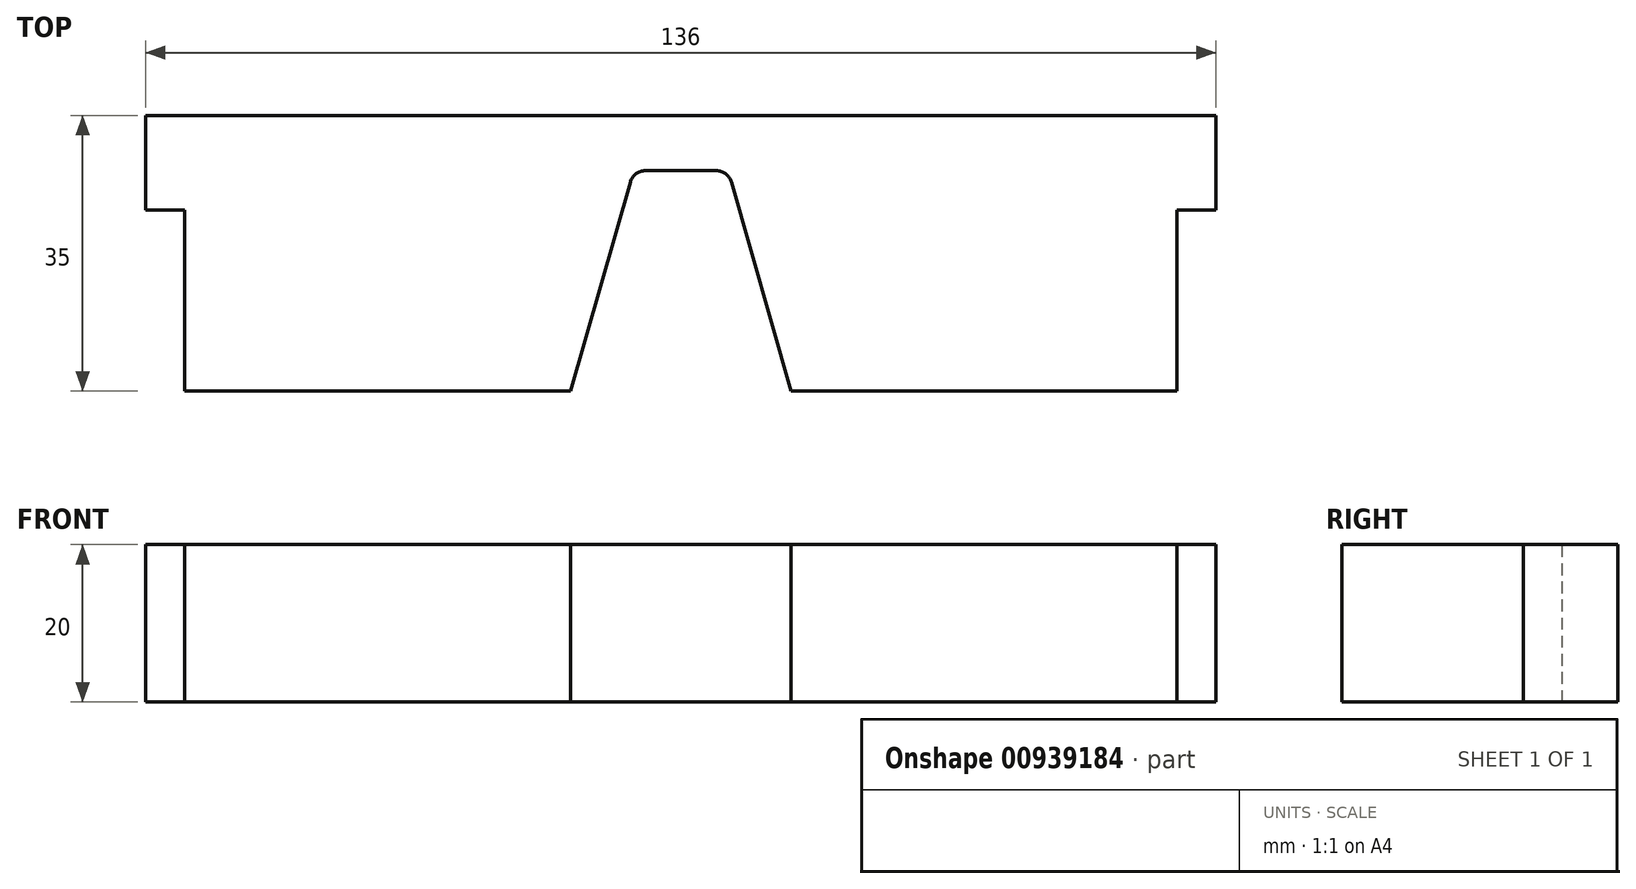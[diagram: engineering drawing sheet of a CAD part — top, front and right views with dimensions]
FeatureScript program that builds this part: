
annotation { "Feature Type Name" : "Feature", "Feature Type Description" : "" }
export const myFeature = defineFeature(function(context is Context, id is Id, definition is map)
    precondition{}
    {
        {
            var Q0;
            Q0=qCreatedBy(makeId("Top.planeOp"),FACE);
            var sketch = newSketch(context, id + "F0", { "sketchPlane" : qUnion([Q0])});
            skLineSegment(sketch, "E0.bottom", {"start": v(0, 0) * mm, "end": v(136, 0) * mm});
            skLineSegment(sketch, "E0.top", {"start": v(0, -35) * mm, "end": v(136, -35) * mm});
            skLineSegment(sketch, "E0.left", {"start": v(0, 0) * mm, "end": v(0, -35) * mm});
            skLineSegment(sketch, "E0.right", {"start": v(136, 0) * mm, "end": v(136, -35) * mm});
            skSolve(sketch);
        }
        {
            var Q0;
            Q0=makeQuery(id+"F0.imprint","IMPRINT",FACE,{"disambiguationData":[TD([[makeQuery(id+"F0.imprint","IMPRINT",EDGE,{"derivedFrom":sQuery(id+"F0.wireOp",EDGE,"E0.bottom")}),-1.0]])]});
            extrude(context, id + "F1", {"entities" : qUnion([Q0]), "depth" : 20 * mm, "offsetDistance" : 25 * mm});
        }
        {
            var Q0;
            Q0=makeQuery(id+"F1.opExtrude","CAP_FACE",FACE,{"disambiguationData":[OSD([sQuery(id+"F0.wireOp",EDGE,"E0.bottom"),sQuery(id+"F0.wireOp",EDGE,"E0.top"),sQuery(id+"F0.wireOp",EDGE,"E0.left"),sQuery(id+"F0.wireOp",EDGE,"E0.right")])],"isStart":false});
            var sketch = newSketch(context, id + "F2", { "sketchPlane" : qUnion([Q0])});
            skLineSegment(sketch, "E1", {"start": v(68, 0) * mm, "end": v(68, -35) * mm, "construction": true});
            skPoint(sketch, "E2", {"position": v(62, 0) * mm});
            skPoint(sketch, "E3", {"position": v(62, -7) * mm});
            skLineSegment(sketch, "E4", {"start": v(62, -7) * mm, "end": v(68, -7) * mm});
            skLineSegment(sketch, "E5", {"start": v(68, -7) * mm, "end": v(68, 0) * mm});
            skLineSegment(sketch, "E6", {"start": v(62, 0) * mm, "end": v(68, 0) * mm});
            skLineSegment(sketch, "E7", {"start": v(0, 0) * mm, "end": v(0, -12) * mm});
            skLineSegment(sketch, "E8", {"start": v(0, -12) * mm, "end": v(5, -12) * mm});
            skLineSegment(sketch, "E9", {"start": v(5, -12) * mm, "end": v(5, -35) * mm});
            skPoint(sketch, "E10", {"position": v(54, -35) * mm});
            skLineSegment(sketch, "E11", {"start": v(62, -7) * mm, "end": v(54, -35) * mm});
            skLineSegment(sketch, "E12", {"start": v(5, -35) * mm, "end": v(54, -35) * mm});
            skLineSegment(sketch, "E13", {"start": v(0, 0) * mm, "end": v(62, 0) * mm});
            skLineSegment(sketch, "E14.MirrorCS", {"start": v(74, 0) * mm, "end": v(68, 0) * mm});
            skLineSegment(sketch, "E15.MirrorCS", {"start": v(74, -7) * mm, "end": v(68, -7) * mm});
            skPoint(sketch, "E16.MirrorP", {"position": v(82, -35) * mm});
            skLineSegment(sketch, "E17.MirrorCS", {"start": v(136, -12) * mm, "end": v(131, -12) * mm});
            skLineSegment(sketch, "E18.MirrorCS", {"start": v(136, 0) * mm, "end": v(74, 0) * mm});
            skLineSegment(sketch, "E19.MirrorCS", {"start": v(131, -35) * mm, "end": v(82, -35) * mm});
            skPoint(sketch, "E20.MirrorP", {"position": v(74, -7) * mm});
            skPoint(sketch, "E21.MirrorP", {"position": v(74, 0) * mm});
            skLineSegment(sketch, "E22.MirrorCS", {"start": v(136, 0) * mm, "end": v(136, -12) * mm});
            skLineSegment(sketch, "E23.MirrorCS", {"start": v(74, -7) * mm, "end": v(82, -35) * mm});
            skLineSegment(sketch, "E24.MirrorCS", {"start": v(131, -12) * mm, "end": v(131, -35) * mm});
            skSolve(sketch);
        }
        {
            var Q0;
            Q0=makeQuery(id+"F2.imprint","IMPRINT",FACE,{"disambiguationData":[TD([[makeQuery(id+"F2.imprint","IMPRINT",EDGE,{"derivedFrom":sQuery(id+"F2.wireOp",EDGE,"E4")}),-1.0]])]});
            var Q1;
            {var subQ0=sQuery(id+"F2.wireOp",EDGE,"E17.MirrorCS");Q1=makeQuery(id+"F2.imprint","IMPRINT",FACE,{"disambiguationData":[TD([[makeQuery(id+"F2.imprint","IMPRINT",EDGE,{"derivedFrom":subQ0}),1.0]])]});}
            var Q2;
            {var subQ0=sQuery(id+"F2.wireOp",EDGE,"E8");Q2=makeQuery(id+"F2.imprint","IMPRINT",FACE,{"disambiguationData":[TD([[makeQuery(id+"F2.imprint","IMPRINT",EDGE,{"derivedFrom":subQ0}),-1.0]])]});}
            extrude(context, id + "F3", {"entities" : qUnion([Q0, Q1, Q2]), "operationType" : NewBodyOperationType.REMOVE, "oppositeDirection" : true, "depth" : 25 * mm, "offsetDistance" : 25 * mm});
        }
        {
            var Q0;
            Q0=makeQuery(id+"F3.boolean.opBoolean","COPY",EDGE,{"derivedFrom":makeQuery(id+"F3.opExtrude","SWEPT_EDGE",EDGE,{"disambiguationData":[OSD([sQuery(id+"F2.wireOp",EDGE,"E4"),sQuery(id+"F2.wireOp",EDGE,"E11")])]})});
            var Q1;
            Q1=makeQuery(id+"F3.boolean.opBoolean","COPY",EDGE,{"derivedFrom":makeQuery(id+"F3.opExtrude","SWEPT_EDGE",EDGE,{"disambiguationData":[OSD([sQuery(id+"F2.wireOp",EDGE,"E15.MirrorCS"),sQuery(id+"F2.wireOp",EDGE,"E23.MirrorCS")])]})});
            fillet(context, id + "F4", {"entities" : qUnion([Q0, Q1]), "radius" : 2 * mm, "tangentPropagation" : true, "allowEdgeOverflow" : false});
        }
    });
